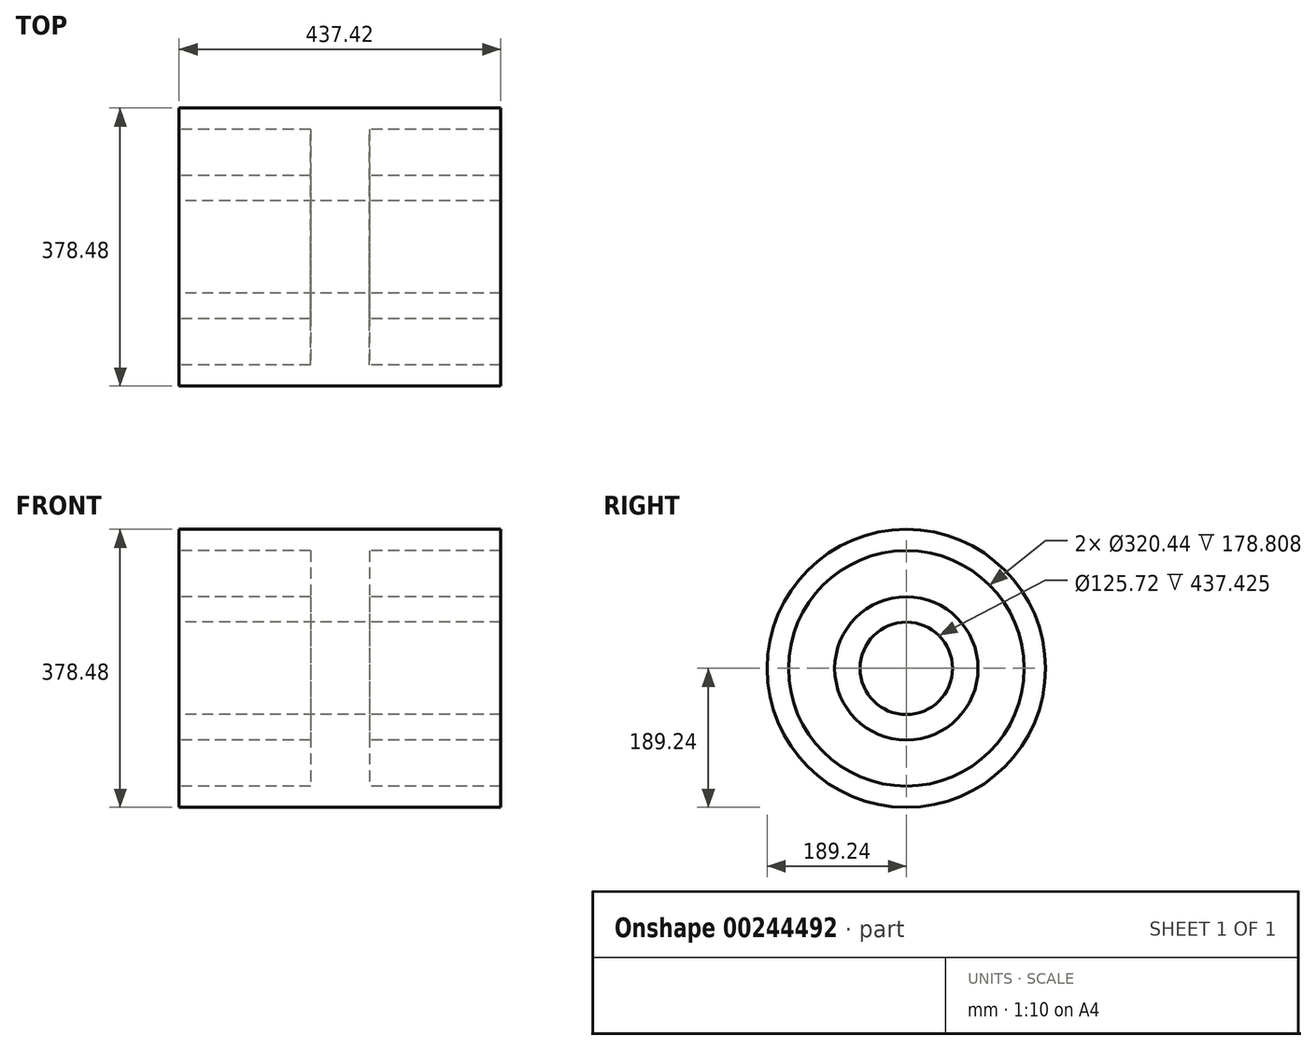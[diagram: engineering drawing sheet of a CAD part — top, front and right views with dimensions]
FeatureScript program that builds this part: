
annotation { "Feature Type Name" : "Feature", "Feature Type Description" : "" }
export const myFeature = defineFeature(function(context is Context, id is Id, definition is map)
    precondition{}
    {
        {
            var Q0;
            Q0=qCreatedBy(makeId("Front.planeOp"),FACE);
            var sketch = newSketch(context, id + "F0", { "sketchPlane" : qUnion([Q0])});
            skLineSegment(sketch, "E0", {"start": v(-115.38, 0) * mm, "end": v(112.43, 0) * mm, "construction": true});
            skLineSegment(sketch, "E1", {"start": v(0, 0) * mm, "end": v(0, 252.9) * mm, "construction": true});
            skLineSegment(sketch, "E2", {"start": v(0, 62.86) * mm, "end": v(218.71, 62.86) * mm});
            skLineSegment(sketch, "E3", {"start": v(218.71, 62.86) * mm, "end": v(218.71, 97.5) * mm});
            skLineSegment(sketch, "E4", {"start": v(218.71, 97.5) * mm, "end": v(39.9, 97.5) * mm});
            skLineSegment(sketch, "E5", {"start": v(39.9, 97.5) * mm, "end": v(39.9, 160.22) * mm});
            skLineSegment(sketch, "E6", {"start": v(39.9, 160.22) * mm, "end": v(218.71, 160.22) * mm});
            skLineSegment(sketch, "E7", {"start": v(218.71, 160.22) * mm, "end": v(218.71, 189.24) * mm});
            skLineSegment(sketch, "E8", {"start": v(218.71, 189.24) * mm, "end": v(0, 189.24) * mm});
            skLineSegment(sketch, "E9.MirrorCS", {"start": v(-218.71, 189.24) * mm, "end": v(0, 189.24) * mm});
            skLineSegment(sketch, "E10.MirrorCS", {"start": v(-39.9, 160.22) * mm, "end": v(-218.71, 160.22) * mm});
            skLineSegment(sketch, "E11.MirrorCS", {"start": v(-39.9, 97.5) * mm, "end": v(-39.9, 160.22) * mm});
            skLineSegment(sketch, "E12.MirrorCS", {"start": v(0, 62.86) * mm, "end": v(-218.71, 62.86) * mm});
            skLineSegment(sketch, "E13.MirrorCS", {"start": v(-218.71, 160.22) * mm, "end": v(-218.71, 189.24) * mm});
            skLineSegment(sketch, "E14.MirrorCS", {"start": v(-218.71, 62.86) * mm, "end": v(-218.71, 97.5) * mm});
            skLineSegment(sketch, "E15.MirrorCS", {"start": v(-218.71, 97.5) * mm, "end": v(-39.9, 97.5) * mm});
            skSolve(sketch);
        }
        {
            var Q0;
            Q0 = qSketchRegion(id + "F0", true);
            var Q1;
            Q1=sQuery(id+"F0.wireOp",EDGE,"E0");
            revolve(context, id + "F1", {"entities" : qUnion([Q0]), "axis" : qUnion([Q1]), "revolveType" : RevolveType.FULL});
        }
    });
